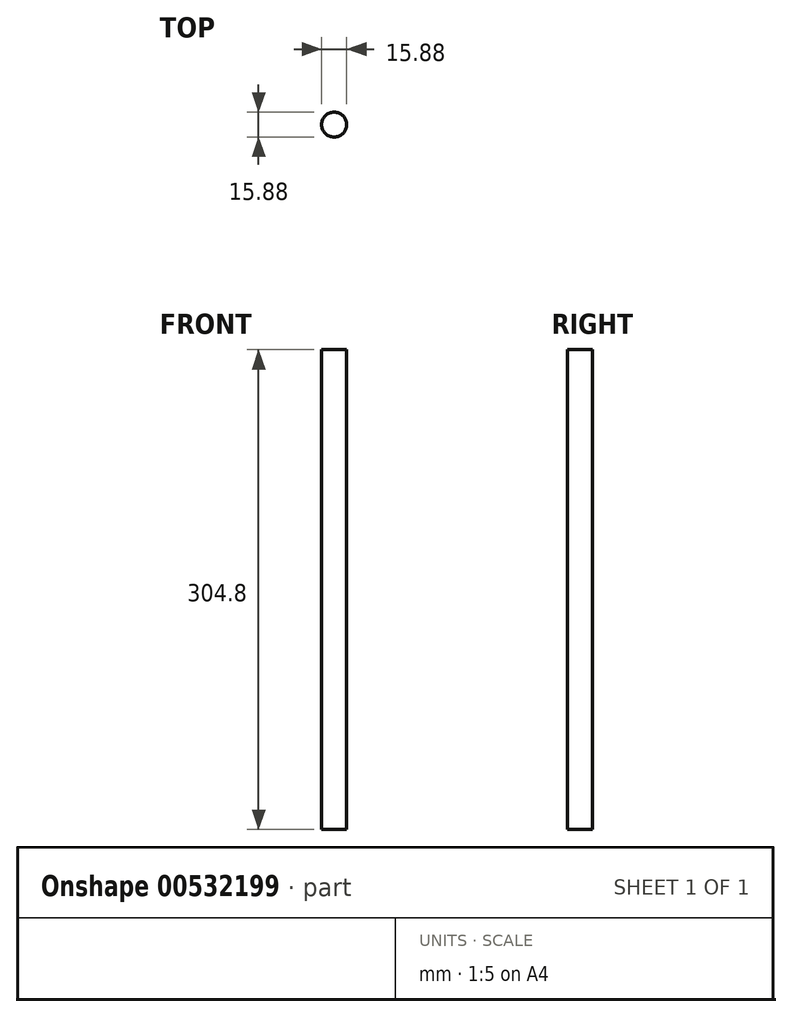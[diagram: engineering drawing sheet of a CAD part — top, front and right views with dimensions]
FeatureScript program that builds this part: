
annotation { "Feature Type Name" : "Feature", "Feature Type Description" : "" }
export const myFeature = defineFeature(function(context is Context, id is Id, definition is map)
    precondition{}
    {
        {
            var Q0;
            Q0=qCreatedBy(makeId("Top.planeOp"),FACE);
            var sketch = newSketch(context, id + "F0", { "sketchPlane" : qUnion([Q0])});
            skCircle(sketch, "E0", {"center": v(0, 0) * mm, "radius": 7.94 * mm});
            skSolve(sketch);
        }
        {
            var Q0;
            Q0 = qSketchRegion(id + "F0", true);
            extrude(context, id + "F1", {"entities" : qUnion([Q0]), "depth" : 304.8 * mm, "offsetDistance" : 25.4 * mm});
        }
    });
